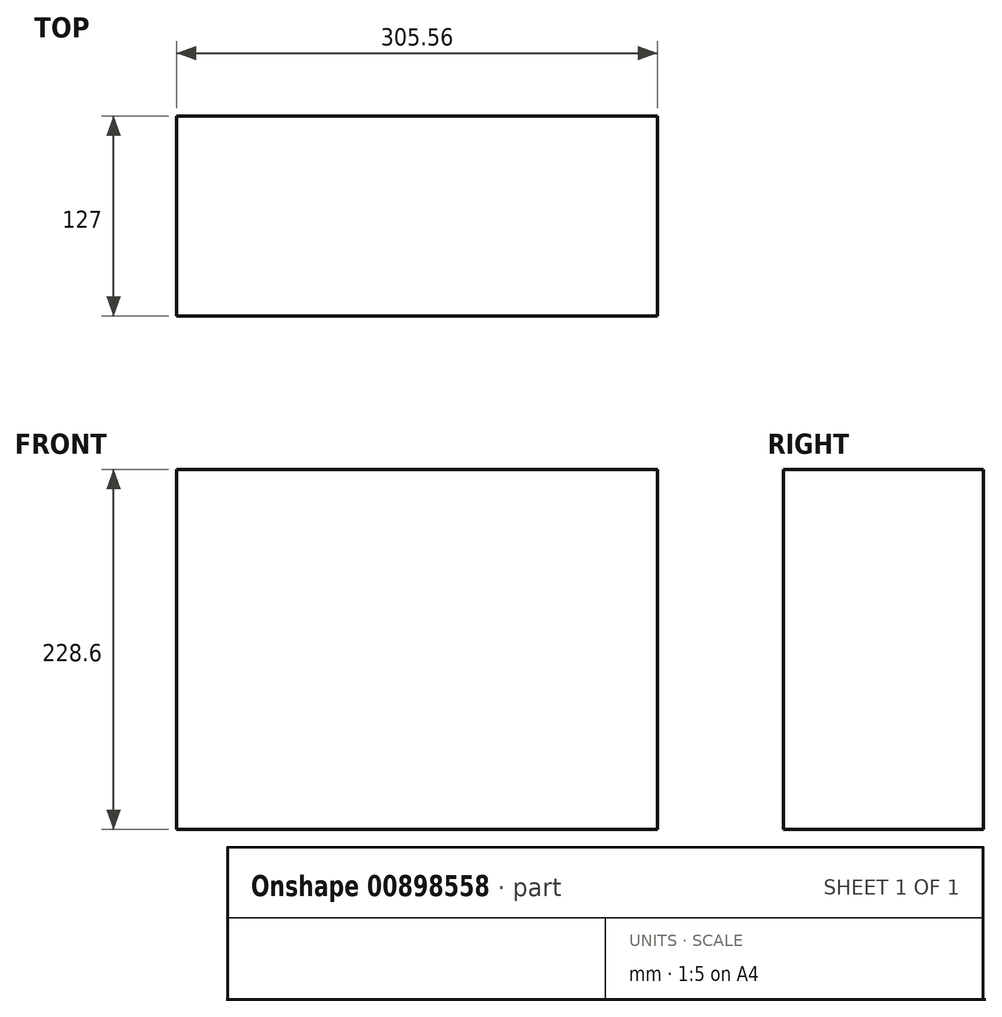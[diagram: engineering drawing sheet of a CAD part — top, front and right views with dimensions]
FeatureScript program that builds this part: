
annotation { "Feature Type Name" : "Feature", "Feature Type Description" : "" }
export const myFeature = defineFeature(function(context is Context, id is Id, definition is map)
    precondition{}
    {
        {
            var Q0;
            Q0=qCreatedBy(makeId("Front.planeOp"),FACE);
            var sketch = newSketch(context, id + "F0", { "sketchPlane" : qUnion([Q0])});
            skLineSegment(sketch, "E0.bottom", {"start": v(-118.97, 13.8) * mm, "end": v(186.6, 13.8) * mm});
            skLineSegment(sketch, "E0.top", {"start": v(-118.97, 101.7) * mm, "end": v(186.6, 101.7) * mm});
            skLineSegment(sketch, "E0.left", {"start": v(-118.97, 13.8) * mm, "end": v(-118.97, 101.7) * mm});
            skLineSegment(sketch, "E0.right", {"start": v(186.6, 13.8) * mm, "end": v(186.6, 101.7) * mm});
            skPoint(sketch, "E0.middle", {"position": v(33.81, 57.75) * mm});
            skSolve(sketch);
        }
        {
            var Q0;
            Q0=sQuery(id+"F0.wireOp",EDGE,"E0.bottom");
            extrude(context, id + "F1", {"bodyType" : ToolBodyType.SURFACE, "surfaceEntities" : qUnion([Q0]), "depth" : 127 * mm, "offsetDistance" : 25.4 * mm});
        }
        {
            var Q0;
            Q0=makeQuery(id+"F1.opExtrude","SWEPT_FACE",FACE,{"disambiguationData":[OSD([sQuery(id+"F0.wireOp",EDGE,"E0.bottom")])]});
            extrude(context, id + "F2", {"entities" : qUnion([Q0]), "depth" : 228.6 * mm, "offsetDistance" : 25.4 * mm});
        }
    });
